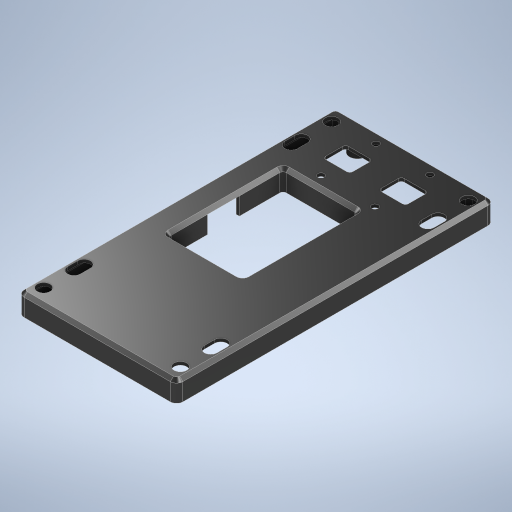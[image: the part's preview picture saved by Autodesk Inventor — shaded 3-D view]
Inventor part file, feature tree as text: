
AUTODESK INVENTOR PART (.ipt)
format: ipt  version: 2024.2 (Build 282272000, 272)  size: 585,728 bytes
history: native  units: mm
features: hole x3, sketch x2, other x1, extrude x1, fillet x1
ambient origin geometry x8: Origin, YZ Plane, XZ Plane, XY Plane, X Axis, Y Axis, Z Axis, Center Point
bodies: Solid1 (feature_tree)
feature tree (8):
  other  "FootSoleFrame.ipt"
  sketch  "Sketch2"  dims[d10=1.0mm d11=1.0mm d27=2.0mm d34=2.0mm d45=2.0mm d46=2.0mm d47=2.0mm d85=11.0mm d86=0.0mm d90=8.0mm d91=6.0mm d92=4.0mm d93=2.0mm d94=90.0deg d95=8.0mm d96=20.594885mm d103=20.0mm d107=4.0mm d108=6.0mm d109=4.0mm d110=2.0mm d111=90.0deg d112=6.0mm d113=0.0mm d115=4.0mm d118=2.0mm d119=2.0mm d120=45.0deg d135=15.0mm d137=2.0mm d138=6.0mm d139=0.0mm d140=6.0mm d141=1.0mm d142=8.0mm d145=12.4mm d146=15.0mm d147=1.0mm d148=1.0mm d150=2.0mm d151=4.0mm d152=6.0mm d153=4.0mm d154=2.0mm d155=90.0deg d156=8.0mm d157=20.594885mm d89=0.0mm d104=0.0mm d105=0.0mm d106=0.0mm d125=1.0mm d126=1.0mm d127=1.0mm d128=0.15mm d129=0.25mm d130=0.375mm d131=14.3117mm d132=0.75mm d133=20.594885mm d134=0.0625mm d136=0.375mm]
  extrude  "Extrusion1"  Depth=13.0mm TaperAngle=0.0deg
  hole  "Phi8.0"  [1 undecoded]
  hole  "Phi4.0-6"  [1 undecoded]
  fillet  "R2(2)"  Radius=2.0mm
  hole  "Phi4.0"  [1 undecoded]
  sketch  "Sketch1"  dims[d0=10.0mm d1=13.0mm d2=0.0mm]
note: 3 required parameter values undecoded (feature->parameter linkage not recoverable at this tier; creation-order binding heuristic only, values carry confidence <= 0.55)
